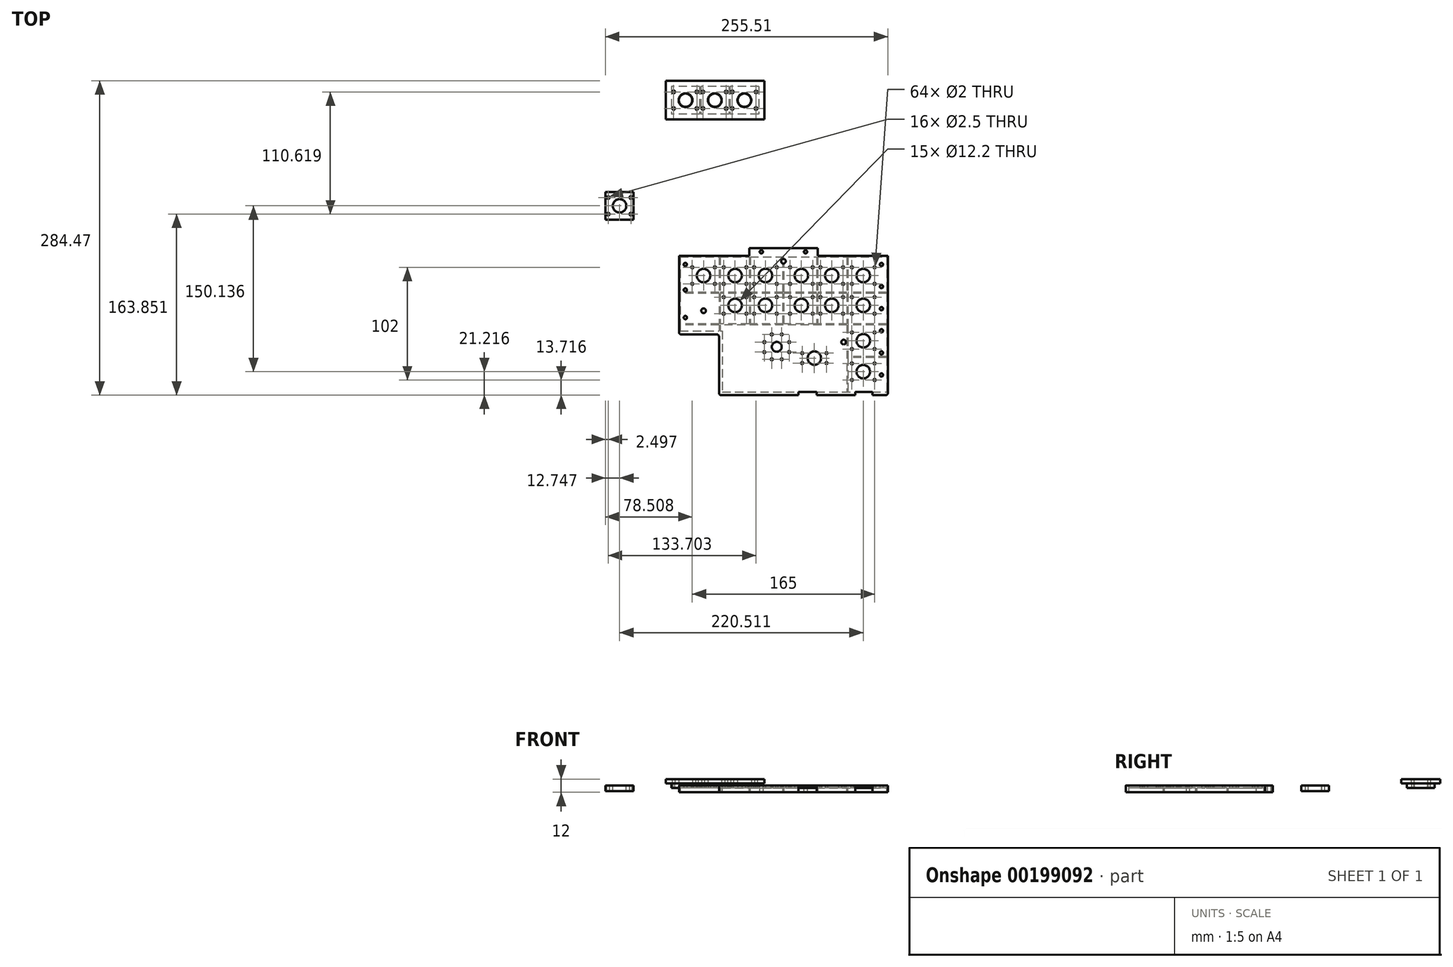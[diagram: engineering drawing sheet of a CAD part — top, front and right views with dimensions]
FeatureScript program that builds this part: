
annotation { "Feature Type Name" : "Feature", "Feature Type Description" : "" }
export const myFeature = defineFeature(function(context is Context, id is Id, definition is map)
    precondition{}
    {
        {
            var Q0;
            Q0=qCreatedBy(makeId("Top.planeOp"),FACE);
            var sketch = newSketch(context, id + "F0", { "sketchPlane" : qUnion([Q0])});
            skLineSegment(sketch, "E0.bottom", {"start": v(7.75, 12.5) * mm, "end": v(-7.75, 12.5) * mm});
            skLineSegment(sketch, "E0.top", {"start": v(7.75, -12.5) * mm, "end": v(-7.75, -12.5) * mm});
            skLineSegment(sketch, "E0.left", {"start": v(7.75, 12.5) * mm, "end": v(7.75, -12.5) * mm});
            skLineSegment(sketch, "E0.right", {"start": v(-7.75, 12.5) * mm, "end": v(-7.75, -12.5) * mm});
            skPoint(sketch, "E0.middle", {"position": v(0, 0) * mm});
            skLineSegment(sketch, "E1.bottom", {"start": v(-7.75, 12.5) * mm, "end": v(-12.75, 12.5) * mm});
            skLineSegment(sketch, "E1.top", {"start": v(-7.75, -12.5) * mm, "end": v(-12.75, -12.5) * mm});
            skLineSegment(sketch, "E1.right", {"start": v(-12.75, 12.5) * mm, "end": v(-12.75, -12.5) * mm});
            skLineSegment(sketch, "E2.bottom", {"start": v(7.75, 12.5) * mm, "end": v(12.75, 12.5) * mm});
            skLineSegment(sketch, "E2.top", {"start": v(7.75, -12.5) * mm, "end": v(12.75, -12.5) * mm});
            skLineSegment(sketch, "E2.right", {"start": v(12.75, 12.5) * mm, "end": v(12.75, -12.5) * mm});
            skCircle(sketch, "E3", {"center": v(-10.75, 7.5) * mm, "radius": 0.9 * mm});
            skPoint(sketch, "E3.centerSnap0", {"position": v(-10.25, 12.5) * mm});
            skCircle(sketch, "E4", {"center": v(-10.75, -7.5) * mm, "radius": 0.9 * mm});
            skCircle(sketch, "E5", {"center": v(10.25, 7.5) * mm, "radius": 0.9 * mm});
            skPoint(sketch, "E5.centerSnap0", {"position": v(10.25, 12.5) * mm});
            skCircle(sketch, "E6", {"center": v(10.25, -7.5) * mm, "radius": 0.9 * mm});
            skCircle(sketch, "E7", {"center": v(0, 0) * mm, "radius": 6 * mm});
            skLineSegment(sketch, "E8.bottom", {"start": v(34.25, 12.5) * mm, "end": v(18.75, 12.5) * mm});
            skLineSegment(sketch, "E8.top", {"start": v(34.25, -12.5) * mm, "end": v(18.75, -12.5) * mm});
            skLineSegment(sketch, "E8.left", {"start": v(34.25, 12.5) * mm, "end": v(34.25, -12.5) * mm});
            skLineSegment(sketch, "E8.right", {"start": v(18.75, 12.5) * mm, "end": v(18.75, -12.5) * mm});
            skPoint(sketch, "E8.middle", {"position": v(26.5, 0) * mm});
            skLineSegment(sketch, "E9.bottom", {"start": v(18.75, 12.5) * mm, "end": v(13.75, 12.5) * mm});
            skLineSegment(sketch, "E9.top", {"start": v(18.75, -12.5) * mm, "end": v(13.75, -12.5) * mm});
            skLineSegment(sketch, "E9.right", {"start": v(13.75, 12.5) * mm, "end": v(13.75, -12.5) * mm});
            skLineSegment(sketch, "E10.bottom", {"start": v(34.25, 12.5) * mm, "end": v(39.25, 12.5) * mm});
            skLineSegment(sketch, "E10.top", {"start": v(34.25, -12.5) * mm, "end": v(39.25, -12.5) * mm});
            skLineSegment(sketch, "E10.right", {"start": v(39.25, 12.5) * mm, "end": v(39.25, -12.5) * mm});
            skCircle(sketch, "E11", {"center": v(15.75, 7.5) * mm, "radius": 0.9 * mm});
            skPoint(sketch, "E11.centerSnap0", {"position": v(16.25, 12.5) * mm});
            skCircle(sketch, "E12", {"center": v(15.75, -7.5) * mm, "radius": 0.9 * mm});
            skCircle(sketch, "E13", {"center": v(36.75, 7.5) * mm, "radius": 0.9 * mm});
            skPoint(sketch, "E13.centerSnap0", {"position": v(36.75, 12.5) * mm});
            skCircle(sketch, "E14", {"center": v(36.75, -7.5) * mm, "radius": 0.9 * mm});
            skCircle(sketch, "E15", {"center": v(26.5, 0) * mm, "radius": 6 * mm});
            skLineSegment(sketch, "E16.bottom", {"start": v(61.25, 12.5) * mm, "end": v(45.25, 12.5) * mm});
            skLineSegment(sketch, "E16.top", {"start": v(61.25, -12.5) * mm, "end": v(45.25, -12.5) * mm});
            skLineSegment(sketch, "E16.left", {"start": v(61.25, 12.5) * mm, "end": v(61.25, -12.5) * mm});
            skLineSegment(sketch, "E16.right", {"start": v(45.25, 12.5) * mm, "end": v(45.25, -12.5) * mm});
            skPoint(sketch, "E16.middle", {"position": v(53.25, 0) * mm});
            skLineSegment(sketch, "E17.bottom", {"start": v(45.25, 12.5) * mm, "end": v(40.25, 12.5) * mm});
            skLineSegment(sketch, "E17.top", {"start": v(45.25, -12.5) * mm, "end": v(40.25, -12.5) * mm});
            skLineSegment(sketch, "E17.right", {"start": v(40.25, 12.5) * mm, "end": v(40.25, -12.5) * mm});
            skLineSegment(sketch, "E18.bottom", {"start": v(61.25, 12.5) * mm, "end": v(66.25, 12.5) * mm});
            skLineSegment(sketch, "E18.top", {"start": v(61.25, -12.5) * mm, "end": v(66.25, -12.5) * mm});
            skLineSegment(sketch, "E18.right", {"start": v(66.25, 12.5) * mm, "end": v(66.25, -12.5) * mm});
            skCircle(sketch, "E19", {"center": v(42.25, 7.5) * mm, "radius": 0.9 * mm});
            skPoint(sketch, "E19.centerSnap0", {"position": v(42.75, 12.5) * mm});
            skCircle(sketch, "E20", {"center": v(42.25, -7.5) * mm, "radius": 0.9 * mm});
            skCircle(sketch, "E21", {"center": v(63.75, 7.5) * mm, "radius": 0.9 * mm});
            skPoint(sketch, "E21.centerSnap0", {"position": v(63.75, 12.5) * mm});
            skCircle(sketch, "E22", {"center": v(63.75, -7.5) * mm, "radius": 0.9 * mm});
            skCircle(sketch, "E23", {"center": v(53.25, 0) * mm, "radius": 6 * mm});
            skSolve(sketch);
        }
        {
            var Q0;
            Q0=makeQuery(id+"F0.imprint","IMPRINT",FACE,{"disambiguationData":[TD([[makeQuery(id+"F0.imprint","IMPRINT",EDGE,{"derivedFrom":sQuery(id+"F0.wireOp",EDGE,"E0.bottom")}),1.0]])]});
            var Q1;
            Q1=makeQuery(id+"F0.imprint","IMPRINT",FACE,{"disambiguationData":[TD([[makeQuery(id+"F0.imprint","IMPRINT",EDGE,{"derivedFrom":sQuery(id+"F0.wireOp",EDGE,"E1.bottom")}),1.0]])]});
            var Q2;
            Q2=makeQuery(id+"F0.imprint","IMPRINT",FACE,{"disambiguationData":[TD([[makeQuery(id+"F0.imprint","IMPRINT",EDGE,{"derivedFrom":sQuery(id+"F0.wireOp",EDGE,"E2.bottom")}),-1.0]])]});
            var Q3;
            Q3=makeQuery(id+"F0.imprint","IMPRINT",FACE,{"disambiguationData":[TD([[makeQuery(id+"F0.imprint","IMPRINT",EDGE,{"derivedFrom":sQuery(id+"F0.wireOp",EDGE,"E9.bottom")}),1.0]])]});
            var Q4;
            Q4=makeQuery(id+"F0.imprint","IMPRINT",FACE,{"disambiguationData":[TD([[makeQuery(id+"F0.imprint","IMPRINT",EDGE,{"derivedFrom":sQuery(id+"F0.wireOp",EDGE,"E8.bottom")}),1.0]])]});
            var Q5;
            Q5=makeQuery(id+"F0.imprint","IMPRINT",FACE,{"disambiguationData":[TD([[makeQuery(id+"F0.imprint","IMPRINT",EDGE,{"derivedFrom":sQuery(id+"F0.wireOp",EDGE,"E10.bottom")}),-1.0]])]});
            var Q6;
            Q6=makeQuery(id+"F0.imprint","IMPRINT",FACE,{"disambiguationData":[TD([[makeQuery(id+"F0.imprint","IMPRINT",EDGE,{"derivedFrom":sQuery(id+"F0.wireOp",EDGE,"E17.bottom")}),1.0]])]});
            var Q7;
            Q7=makeQuery(id+"F0.imprint","IMPRINT",FACE,{"disambiguationData":[TD([[makeQuery(id+"F0.imprint","IMPRINT",EDGE,{"derivedFrom":sQuery(id+"F0.wireOp",EDGE,"E16.bottom")}),1.0]])]});
            var Q8;
            Q8=makeQuery(id+"F0.imprint","IMPRINT",FACE,{"disambiguationData":[TD([[makeQuery(id+"F0.imprint","IMPRINT",EDGE,{"derivedFrom":sQuery(id+"F0.wireOp",EDGE,"E18.bottom")}),-1.0]])]});
            extrude(context, id + "F1", {"entities" : qUnion([Q0, Q1, Q2, Q3, Q4, Q5, Q6, Q7, Q8]), "depth" : 4 * mm});
        }
        {
            var Q0;
            Q0=makeQuery(id+"F1.opExtrude","CAP_FACE",FACE,{"disambiguationData":[OSD([sQuery(id+"F0.wireOp",EDGE,"E0.bottom"),sQuery(id+"F0.wireOp",EDGE,"E0.top"),sQuery(id+"F0.wireOp",EDGE,"E1.bottom"),sQuery(id+"F0.wireOp",EDGE,"E1.top"),sQuery(id+"F0.wireOp",EDGE,"E1.right"),sQuery(id+"F0.wireOp",EDGE,"E2.bottom"),sQuery(id+"F0.wireOp",EDGE,"E2.top"),sQuery(id+"F0.wireOp",EDGE,"E2.right"),sQuery(id+"F0.wireOp",EDGE,"E3"),sQuery(id+"F0.wireOp",EDGE,"E4"),sQuery(id+"F0.wireOp",EDGE,"E5"),sQuery(id+"F0.wireOp",EDGE,"E6"),sQuery(id+"F0.wireOp",EDGE,"E7")])],"isStart":false});
            var sketch = newSketch(context, id + "F2", { "sketchPlane" : qUnion([Q0])});
            skLineSegment(sketch, "E24.bottom", {"start": v(-17.75, 17.5) * mm, "end": v(71.25, 17.5) * mm});
            skLineSegment(sketch, "E24.top", {"start": v(-17.75, -17.5) * mm, "end": v(71.25, -17.5) * mm});
            skLineSegment(sketch, "E24.left", {"start": v(-17.75, 17.5) * mm, "end": v(-17.75, -17.5) * mm});
            skLineSegment(sketch, "E24.right", {"start": v(71.25, 17.5) * mm, "end": v(71.25, -17.5) * mm});
            skCircle(sketch, "E25", {"center": v(-10.75, 7.5) * mm, "radius": 1.25 * mm});
            skCircle(sketch, "E26", {"center": v(-10.75, -7.5) * mm, "radius": 1.25 * mm});
            skCircle(sketch, "E27", {"center": v(10.25, -7.5) * mm, "radius": 1.25 * mm});
            skCircle(sketch, "E28", {"center": v(10.25, 7.5) * mm, "radius": 1.25 * mm});
            skCircle(sketch, "E29", {"center": v(15.75, 7.5) * mm, "radius": 1.25 * mm});
            skCircle(sketch, "E30", {"center": v(15.75, -7.5) * mm, "radius": 1.25 * mm});
            skCircle(sketch, "E31", {"center": v(36.75, -7.5) * mm, "radius": 1.25 * mm});
            skCircle(sketch, "E32", {"center": v(0, 0) * mm, "radius": 6.25 * mm});
            skCircle(sketch, "E33", {"center": v(26.5, 0) * mm, "radius": 6.25 * mm});
            skCircle(sketch, "E34", {"center": v(53.25, 0) * mm, "radius": 6.25 * mm});
            skCircle(sketch, "E35", {"center": v(36.75, 7.5) * mm, "radius": 1.25 * mm});
            skCircle(sketch, "E36", {"center": v(42.25, 7.5) * mm, "radius": 1.25 * mm});
            skCircle(sketch, "E37", {"center": v(42.25, -7.5) * mm, "radius": 1.25 * mm});
            skCircle(sketch, "E38", {"center": v(63.75, 7.5) * mm, "radius": 1.25 * mm});
            skCircle(sketch, "E39", {"center": v(63.75, -7.5) * mm, "radius": 1.25 * mm});
            skSolve(sketch);
        }
        {
            var Q0;
            Q0=qSketchRegion(id+"F2",true);
            extrude(context, id + "F3", {"entities" : qUnion([Q0]), "depth" : 4 * mm});
        }
        {
            var Q0;
            Q0=qCreatedBy(makeId("Top.planeOp"),FACE);
            var sketch = newSketch(context, id + "F4", { "sketchPlane" : qUnion([Q0])});
            skLineSegment(sketch, "E40.bottom", {"start": v(3.56, -143.75) * mm, "end": v(29.06, -143.75) * mm, "construction": true});
            skLineSegment(sketch, "E40.top", {"start": v(3.56, -173.75) * mm, "end": v(29.06, -173.75) * mm, "construction": true});
            skLineSegment(sketch, "E40.left", {"start": v(3.56, -143.75) * mm, "end": v(3.56, -173.75) * mm, "construction": true});
            skLineSegment(sketch, "E40.right", {"start": v(29.06, -143.75) * mm, "end": v(29.06, -173.75) * mm, "construction": true});
            skLineSegment(sketch, "E41.bottom", {"start": v(32.06, -143.75) * mm, "end": v(57.56, -143.75) * mm, "construction": true});
            skLineSegment(sketch, "E41.top", {"start": v(32.06, -173.75) * mm, "end": v(57.56, -173.75) * mm, "construction": true});
            skLineSegment(sketch, "E41.left", {"start": v(32.06, -143.75) * mm, "end": v(32.06, -173.75) * mm, "construction": true});
            skLineSegment(sketch, "E41.right", {"start": v(57.56, -143.75) * mm, "end": v(57.56, -173.75) * mm, "construction": true});
            skLineSegment(sketch, "E42.bottom", {"start": v(119.56, -143.75) * mm, "end": v(145.06, -143.75) * mm, "construction": true});
            skLineSegment(sketch, "E42.top", {"start": v(119.56, -173.75) * mm, "end": v(145.06, -173.75) * mm, "construction": true});
            skLineSegment(sketch, "E42.left", {"start": v(119.56, -143.75) * mm, "end": v(119.56, -173.75) * mm, "construction": true});
            skLineSegment(sketch, "E42.right", {"start": v(145.06, -143.75) * mm, "end": v(145.06, -173.75) * mm, "construction": true});
            skLineSegment(sketch, "E43.bottom", {"start": v(148.06, -143.75) * mm, "end": v(173.56, -143.75) * mm, "construction": true});
            skLineSegment(sketch, "E43.top", {"start": v(148.06, -173.75) * mm, "end": v(173.56, -173.75) * mm, "construction": true});
            skLineSegment(sketch, "E43.left", {"start": v(148.06, -143.75) * mm, "end": v(148.06, -173.75) * mm, "construction": true});
            skLineSegment(sketch, "E43.right", {"start": v(173.56, -143.75) * mm, "end": v(173.56, -173.75) * mm, "construction": true});
            skLineSegment(sketch, "E44.top", {"start": v(148.06, -206.75) * mm, "end": v(173.56, -206.75) * mm, "construction": true});
            skLineSegment(sketch, "E45.bottom", {"start": v(148.06, -209.25) * mm, "end": v(173.56, -209.25) * mm, "construction": true});
            skLineSegment(sketch, "E45.top", {"start": v(148.06, -239.25) * mm, "end": v(173.56, -239.25) * mm, "construction": true});
            skLineSegment(sketch, "E45.left", {"start": v(148.06, -209.25) * mm, "end": v(148.06, -239.25) * mm, "construction": true});
            skLineSegment(sketch, "E45.right", {"start": v(173.56, -209.25) * mm, "end": v(173.56, -239.25) * mm, "construction": true});
            skLineSegment(sketch, "E46.bottom", {"start": v(-4.94, -140.75) * mm, "end": v(182.06, -140.75) * mm});
            skLineSegment(sketch, "E46.top", {"start": v(33.28, -263.97) * mm, "end": v(182.06, -263.97) * mm});
            skLineSegment(sketch, "E46.left", {"start": v(-4.94, -140.75) * mm, "end": v(-4.94, -208.97) * mm});
            skLineSegment(sketch, "E46.right", {"start": v(182.06, -140.75) * mm, "end": v(182.06, -263.97) * mm});
            skLineSegment(sketch, "E47", {"start": v(-4.94, -208.97) * mm, "end": v(33.28, -208.97) * mm});
            skLineSegment(sketch, "E48", {"start": v(33.28, -208.97) * mm, "end": v(33.28, -263.97) * mm});
            skLineSegment(sketch, "E49.bottom", {"start": v(-67.45, -83.12) * mm, "end": v(-51.95, -83.12) * mm});
            skLineSegment(sketch, "E49.top", {"start": v(-67.45, -108.12) * mm, "end": v(-51.95, -108.12) * mm});
            skLineSegment(sketch, "E49.left", {"start": v(-67.45, -83.12) * mm, "end": v(-67.45, -108.12) * mm});
            skLineSegment(sketch, "E49.right", {"start": v(-51.95, -83.12) * mm, "end": v(-51.95, -108.12) * mm});
            skLineSegment(sketch, "E50.bottom", {"start": v(-51.95, -83.12) * mm, "end": v(-46.95, -83.12) * mm});
            skLineSegment(sketch, "E50.top", {"start": v(-51.95, -108.12) * mm, "end": v(-46.95, -108.12) * mm});
            skLineSegment(sketch, "E50.right", {"start": v(-46.95, -83.12) * mm, "end": v(-46.95, -108.12) * mm});
            skLineSegment(sketch, "E51.bottom", {"start": v(-67.45, -83.12) * mm, "end": v(-72.45, -83.12) * mm});
            skLineSegment(sketch, "E51.top", {"start": v(-67.45, -108.12) * mm, "end": v(-72.45, -108.12) * mm});
            skLineSegment(sketch, "E51.right", {"start": v(-72.45, -83.12) * mm, "end": v(-72.45, -108.12) * mm});
            skCircle(sketch, "E52", {"center": v(-59.7, -95.62) * mm, "radius": 6.1 * mm});
            skPoint(sketch, "E52.centerSnap0", {"position": v(-67.45, -95.62) * mm});
            skPoint(sketch, "E52.centerSnap1", {"position": v(-59.7, -83.12) * mm});
            skCircle(sketch, "E53", {"center": v(-69.95, -88.12) * mm, "radius": 1.25 * mm});
            skPoint(sketch, "E53.centerSnap0", {"position": v(-69.95, -83.12) * mm});
            skCircle(sketch, "E54", {"center": v(-69.95, -103.12) * mm, "radius": 1.25 * mm});
            skCircle(sketch, "E55", {"center": v(-49.45, -88.12) * mm, "radius": 1.25 * mm});
            skPoint(sketch, "E55.centerSnap0", {"position": v(-49.45, -83.12) * mm});
            skCircle(sketch, "E56", {"center": v(-49.45, -103.12) * mm, "radius": 1.25 * mm});
            skLineSegment(sketch, "E57.bottom", {"start": v(3.56, -146.25) * mm, "end": v(8.56, -146.25) * mm, "construction": true});
            skLineSegment(sketch, "E57.top", {"start": v(3.56, -171.25) * mm, "end": v(8.56, -171.25) * mm, "construction": true});
            skLineSegment(sketch, "E57.left", {"start": v(3.56, -146.25) * mm, "end": v(3.56, -171.25) * mm, "construction": true});
            skLineSegment(sketch, "E57.right", {"start": v(8.56, -146.25) * mm, "end": v(8.56, -171.25) * mm, "construction": true});
            skLineSegment(sketch, "E58.bottom", {"start": v(29.06, -146.25) * mm, "end": v(24.06, -146.25) * mm, "construction": true});
            skLineSegment(sketch, "E58.top", {"start": v(29.06, -171.25) * mm, "end": v(24.06, -171.25) * mm, "construction": true});
            skLineSegment(sketch, "E58.left", {"start": v(29.06, -146.25) * mm, "end": v(29.06, -171.25) * mm, "construction": true});
            skLineSegment(sketch, "E58.right", {"start": v(24.06, -146.25) * mm, "end": v(24.06, -171.25) * mm, "construction": true});
            skCircle(sketch, "E59", {"center": v(6.06, -151.25) * mm, "radius": 1 * mm});
            skPoint(sketch, "E59.centerSnap0", {"position": v(6.06, -146.25) * mm});
            skCircle(sketch, "E60", {"center": v(6.06, -166.25) * mm, "radius": 1 * mm});
            skCircle(sketch, "E61", {"center": v(16.3, -158.75) * mm, "radius": 6.1 * mm});
            skPoint(sketch, "E61.centerSnap0", {"position": v(8.56, -158.75) * mm});
            skPoint(sketch, "E61.centerSnap1", {"position": v(16.3, -143.75) * mm});
            skCircle(sketch, "E62", {"center": v(26.56, -151.25) * mm, "radius": 1 * mm});
            skPoint(sketch, "E62.centerSnap0", {"position": v(26.56, -146.25) * mm});
            skCircle(sketch, "E63", {"center": v(26.56, -166.25) * mm, "radius": 1 * mm});
            skCircle(sketch, "E64", {"center": v(105.56, -228.97) * mm, "radius": 1 * mm});
            skCircle(sketch, "E65", {"center": v(105.56, -237.97) * mm, "radius": 1 * mm});
            skCircle(sketch, "E66", {"center": v(127.56, -228.97) * mm, "radius": 1 * mm});
            skCircle(sketch, "E67", {"center": v(127.56, -237.97) * mm, "radius": 1 * mm});
            skLineSegment(sketch, "E68.bottom", {"start": v(151.56, -240.25) * mm, "end": v(173.56, -240.25) * mm, "construction": true});
            skLineSegment(sketch, "E68.top", {"start": v(151.56, -262.25) * mm, "end": v(173.56, -262.25) * mm, "construction": true});
            skLineSegment(sketch, "E68.left", {"start": v(151.56, -240.25) * mm, "end": v(151.56, -262.25) * mm, "construction": true});
            skLineSegment(sketch, "E68.right", {"start": v(173.56, -240.25) * mm, "end": v(173.56, -262.25) * mm, "construction": true});
            skLineSegment(sketch, "E69.bottom", {"start": v(154.8, -239.75) * mm, "end": v(166.8, -239.75) * mm, "construction": true});
            skLineSegment(sketch, "E69.top", {"start": v(154.8, -251.75) * mm, "end": v(166.8, -251.75) * mm, "construction": true});
            skLineSegment(sketch, "E69.left", {"start": v(154.8, -239.75) * mm, "end": v(154.8, -251.75) * mm, "construction": true});
            skLineSegment(sketch, "E69.right", {"start": v(166.8, -239.75) * mm, "end": v(166.8, -251.75) * mm, "construction": true});
            skLineSegment(sketch, "E70.bottom", {"start": v(32.06, -146.25) * mm, "end": v(37.06, -146.25) * mm, "construction": true});
            skLineSegment(sketch, "E70.top", {"start": v(32.06, -171.25) * mm, "end": v(37.06, -171.25) * mm, "construction": true});
            skLineSegment(sketch, "E70.left", {"start": v(32.06, -146.25) * mm, "end": v(32.06, -171.25) * mm, "construction": true});
            skLineSegment(sketch, "E70.right", {"start": v(37.06, -146.25) * mm, "end": v(37.06, -171.25) * mm, "construction": true});
            skLineSegment(sketch, "E71.bottom", {"start": v(57.56, -146.25) * mm, "end": v(52.56, -146.25) * mm, "construction": true});
            skLineSegment(sketch, "E71.top", {"start": v(57.56, -171.25) * mm, "end": v(52.56, -171.25) * mm, "construction": true});
            skLineSegment(sketch, "E71.left", {"start": v(57.56, -146.25) * mm, "end": v(57.56, -171.25) * mm, "construction": true});
            skLineSegment(sketch, "E71.right", {"start": v(52.56, -146.25) * mm, "end": v(52.56, -171.25) * mm, "construction": true});
            skCircle(sketch, "E72", {"center": v(34.56, -151.25) * mm, "radius": 1 * mm});
            skPoint(sketch, "E72.centerSnap0", {"position": v(34.56, -146.25) * mm});
            skCircle(sketch, "E73", {"center": v(34.56, -166.25) * mm, "radius": 1 * mm});
            skCircle(sketch, "E74", {"center": v(55.06, -151.25) * mm, "radius": 1 * mm});
            skPoint(sketch, "E74.centerSnap0", {"position": v(55.06, -146.25) * mm});
            skCircle(sketch, "E75", {"center": v(55.06, -166.25) * mm, "radius": 1 * mm});
            skCircle(sketch, "E76", {"center": v(44.8, -158.75) * mm, "radius": 6.1 * mm});
            skPoint(sketch, "E76.centerSnap0", {"position": v(37.06, -158.75) * mm});
            skPoint(sketch, "E76.centerSnap1", {"position": v(44.8, -143.75) * mm});
            skLineSegment(sketch, "E77.bottom", {"start": v(119.56, -146.25) * mm, "end": v(124.56, -146.25) * mm, "construction": true});
            skLineSegment(sketch, "E77.top", {"start": v(119.56, -171.25) * mm, "end": v(124.56, -171.25) * mm, "construction": true});
            skLineSegment(sketch, "E77.left", {"start": v(119.56, -146.25) * mm, "end": v(119.56, -171.25) * mm, "construction": true});
            skLineSegment(sketch, "E77.right", {"start": v(124.56, -146.25) * mm, "end": v(124.56, -171.25) * mm, "construction": true});
            skLineSegment(sketch, "E78.bottom", {"start": v(145.06, -146.25) * mm, "end": v(140.06, -146.25) * mm, "construction": true});
            skLineSegment(sketch, "E78.top", {"start": v(145.06, -171.25) * mm, "end": v(140.06, -171.25) * mm, "construction": true});
            skLineSegment(sketch, "E78.left", {"start": v(145.06, -146.25) * mm, "end": v(145.06, -171.25) * mm, "construction": true});
            skLineSegment(sketch, "E78.right", {"start": v(140.06, -146.25) * mm, "end": v(140.06, -171.25) * mm, "construction": true});
            skLineSegment(sketch, "E79.bottom", {"start": v(148.06, -146.25) * mm, "end": v(153.06, -146.25) * mm, "construction": true});
            skLineSegment(sketch, "E79.top", {"start": v(148.06, -171.25) * mm, "end": v(153.06, -171.25) * mm, "construction": true});
            skLineSegment(sketch, "E79.left", {"start": v(148.06, -146.25) * mm, "end": v(148.06, -171.25) * mm, "construction": true});
            skLineSegment(sketch, "E79.right", {"start": v(153.06, -146.25) * mm, "end": v(153.06, -171.25) * mm, "construction": true});
            skLineSegment(sketch, "E80.bottom", {"start": v(173.56, -146.25) * mm, "end": v(168.56, -146.25) * mm, "construction": true});
            skLineSegment(sketch, "E80.top", {"start": v(173.56, -171.25) * mm, "end": v(168.56, -171.25) * mm, "construction": true});
            skLineSegment(sketch, "E80.left", {"start": v(173.56, -146.25) * mm, "end": v(173.56, -171.25) * mm, "construction": true});
            skLineSegment(sketch, "E80.right", {"start": v(168.56, -146.25) * mm, "end": v(168.56, -171.25) * mm, "construction": true});
            skLineSegment(sketch, "E81.top", {"start": v(148.06, -204.25) * mm, "end": v(153.06, -204.25) * mm, "construction": true});
            skLineSegment(sketch, "E82.top", {"start": v(173.56, -204.25) * mm, "end": v(168.56, -204.25) * mm, "construction": true});
            skLineSegment(sketch, "E83.bottom", {"start": v(148.06, -205.25) * mm, "end": v(153.06, -205.25) * mm, "construction": true});
            skLineSegment(sketch, "E83.top", {"start": v(148.06, -230.25) * mm, "end": v(153.06, -230.25) * mm, "construction": true});
            skLineSegment(sketch, "E83.left", {"start": v(148.06, -205.25) * mm, "end": v(148.06, -230.25) * mm, "construction": true});
            skLineSegment(sketch, "E83.right", {"start": v(153.06, -205.25) * mm, "end": v(153.06, -230.25) * mm, "construction": true});
            skLineSegment(sketch, "E84.bottom", {"start": v(173.56, -205.25) * mm, "end": v(168.56, -205.25) * mm, "construction": true});
            skLineSegment(sketch, "E84.top", {"start": v(173.56, -230.25) * mm, "end": v(168.56, -230.25) * mm, "construction": true});
            skLineSegment(sketch, "E84.left", {"start": v(173.56, -205.25) * mm, "end": v(173.56, -230.25) * mm, "construction": true});
            skLineSegment(sketch, "E84.right", {"start": v(168.56, -205.25) * mm, "end": v(168.56, -230.25) * mm, "construction": true});
            skCircle(sketch, "E85", {"center": v(62.06, -178.25) * mm, "radius": 1 * mm});
            skCircle(sketch, "E86", {"center": v(62.06, -193.25) * mm, "radius": 1 * mm});
            skCircle(sketch, "E87", {"center": v(82.56, -178.25) * mm, "radius": 1 * mm});
            skCircle(sketch, "E88", {"center": v(82.56, -193.25) * mm, "radius": 1 * mm});
            skCircle(sketch, "E89", {"center": v(72.3, -185.75) * mm, "radius": 6.1 * mm});
            skCircle(sketch, "E90", {"center": v(82.56, -223.25) * mm, "radius": 4.5 * mm});
            skCircle(sketch, "E91", {"center": v(71.3, -219) * mm, "radius": 1 * mm});
            skCircle(sketch, "E92", {"center": v(71.3, -228) * mm, "radius": 1 * mm});
            skCircle(sketch, "E93", {"center": v(93.8, -219) * mm, "radius": 1 * mm});
            skCircle(sketch, "E94", {"center": v(93.8, -228) * mm, "radius": 1 * mm});
            skCircle(sketch, "E95", {"center": v(94.56, -178.25) * mm, "radius": 1 * mm});
            skCircle(sketch, "E96", {"center": v(94.56, -193.25) * mm, "radius": 1 * mm});
            skCircle(sketch, "E97", {"center": v(115.06, -178.25) * mm, "radius": 1 * mm});
            skCircle(sketch, "E98", {"center": v(115.06, -193.25) * mm, "radius": 1 * mm});
            skCircle(sketch, "E99", {"center": v(122.06, -151.25) * mm, "radius": 1 * mm});
            skPoint(sketch, "E99.centerSnap0", {"position": v(122.06, -146.25) * mm});
            skCircle(sketch, "E100", {"center": v(122.06, -166.25) * mm, "radius": 1 * mm});
            skCircle(sketch, "E101", {"center": v(132.3, -158.75) * mm, "radius": 6.1 * mm});
            skPoint(sketch, "E101.centerSnap0", {"position": v(124.56, -158.75) * mm});
            skPoint(sketch, "E101.centerSnap1", {"position": v(132.3, -143.75) * mm});
            skCircle(sketch, "E102", {"center": v(142.56, -151.25) * mm, "radius": 1 * mm});
            skPoint(sketch, "E102.centerSnap0", {"position": v(142.56, -146.25) * mm});
            skCircle(sketch, "E103", {"center": v(142.56, -166.25) * mm, "radius": 1 * mm});
            skCircle(sketch, "E104", {"center": v(150.56, -151.25) * mm, "radius": 1 * mm});
            skPoint(sketch, "E104.centerSnap0", {"position": v(150.56, -146.25) * mm});
            skCircle(sketch, "E105", {"center": v(150.56, -166.25) * mm, "radius": 1 * mm});
            skCircle(sketch, "E106", {"center": v(171.06, -151.25) * mm, "radius": 1 * mm});
            skPoint(sketch, "E106.centerSnap0", {"position": v(171.06, -146.25) * mm});
            skCircle(sketch, "E107", {"center": v(171.06, -166.25) * mm, "radius": 1 * mm});
            skCircle(sketch, "E108", {"center": v(160.8, -158.75) * mm, "radius": 6.1 * mm});
            skPoint(sketch, "E108.centerSnap0", {"position": v(153.06, -158.75) * mm});
            skPoint(sketch, "E108.centerSnap1", {"position": v(160.8, -143.75) * mm});
            skCircle(sketch, "E109", {"center": v(16.3, -190.57) * mm, "radius": 2.1 * mm});
            skCircle(sketch, "E110", {"center": v(143.06, -218.97) * mm, "radius": 2.1 * mm});
            skCircle(sketch, "E111", {"center": v(150.56, -210.25) * mm, "radius": 1 * mm});
            skPoint(sketch, "E111.centerSnap0", {"position": v(150.56, -205.25) * mm});
            skCircle(sketch, "E112", {"center": v(150.56, -225.25) * mm, "radius": 1 * mm});
            skCircle(sketch, "E113", {"center": v(171.06, -210.25) * mm, "radius": 1 * mm});
            skPoint(sketch, "E113.centerSnap0", {"position": v(171.06, -205.25) * mm});
            skCircle(sketch, "E114", {"center": v(171.06, -225.25) * mm, "radius": 1 * mm});
            skCircle(sketch, "E115", {"center": v(160.8, -217.75) * mm, "radius": 6.1 * mm});
            skPoint(sketch, "E115.centerSnap0", {"position": v(153.06, -217.75) * mm});
            skCircle(sketch, "E116", {"center": v(160.8, -245.75) * mm, "radius": 6.1 * mm});
            skPoint(sketch, "E116.centerSnap0", {"position": v(160.8, -239.75) * mm});
            skPoint(sketch, "E116.centerSnap1", {"position": v(154.8, -245.75) * mm});
            skCircle(sketch, "E117", {"center": v(-0.2, -148.75) * mm, "radius": 1.5 * mm});
            skCircle(sketch, "E118", {"center": v(-0.2, -171.75) * mm, "radius": 1.5 * mm});
            skCircle(sketch, "E119", {"center": v(177.3, -208.75) * mm, "radius": 1.5 * mm});
            skCircle(sketch, "E120", {"center": v(177.3, -228.75) * mm, "radius": 1.5 * mm});
            skCircle(sketch, "E121", {"center": v(177.3, -248.75) * mm, "radius": 1.5 * mm});
            skCircle(sketch, "E122", {"center": v(177.3, -168.75) * mm, "radius": 1.5 * mm});
            skCircle(sketch, "E123", {"center": v(177.3, -188.75) * mm, "radius": 1.5 * mm});
            skCircle(sketch, "E124", {"center": v(177.3, -148.75) * mm, "radius": 1.5 * mm});
            skCircle(sketch, "E125", {"center": v(150.56, -238.25) * mm, "radius": 1 * mm});
            skCircle(sketch, "E126", {"center": v(150.56, -253.25) * mm, "radius": 1 * mm});
            skCircle(sketch, "E127", {"center": v(171.06, -238.25) * mm, "radius": 1 * mm});
            skCircle(sketch, "E128", {"center": v(171.06, -253.25) * mm, "radius": 1 * mm});
            skCircle(sketch, "E129", {"center": v(-0.2, -196.75) * mm, "radius": 1.5 * mm});
            skLineSegment(sketch, "E130.bottom", {"start": v(58.56, -140.75) * mm, "end": v(118.56, -140.75) * mm});
            skLineSegment(sketch, "E130.top", {"start": v(58.56, -133.75) * mm, "end": v(118.56, -133.75) * mm});
            skLineSegment(sketch, "E130.left", {"start": v(58.56, -140.75) * mm, "end": v(58.56, -133.75) * mm});
            skLineSegment(sketch, "E130.right", {"start": v(118.56, -140.75) * mm, "end": v(118.56, -133.75) * mm});
            skCircle(sketch, "E131", {"center": v(68.56, -137.25) * mm, "radius": 1.5 * mm});
            skCircle(sketch, "E132", {"center": v(108.56, -137.25) * mm, "radius": 1.5 * mm});
            skCircle(sketch, "E133", {"center": v(116.56, -233.47) * mm, "radius": 6.1 * mm});
            skCircle(sketch, "E134", {"center": v(82.56, -223.25) * mm, "radius": 12.5 * mm, "construction": true});
            skCircle(sketch, "E135", {"center": v(44.8, -185.75) * mm, "radius": 6.1 * mm});
            skCircle(sketch, "E136", {"center": v(34.56, -178.25) * mm, "radius": 1 * mm});
            skCircle(sketch, "E137", {"center": v(34.56, -193.25) * mm, "radius": 1 * mm});
            skCircle(sketch, "E138", {"center": v(55.06, -178.25) * mm, "radius": 1 * mm});
            skCircle(sketch, "E139", {"center": v(55.06, -193.25) * mm, "radius": 1 * mm});
            skCircle(sketch, "E140", {"center": v(122.06, -193.25) * mm, "radius": 1 * mm});
            skCircle(sketch, "E141", {"center": v(142.56, -193.25) * mm, "radius": 1 * mm});
            skLineSegment(sketch, "E142", {"start": v(223.04, -262.25) * mm, "end": v(194.25, -262.25) * mm, "construction": true});
            skCircle(sketch, "E143", {"center": v(78.06, -212) * mm, "radius": 1 * mm});
            skCircle(sketch, "E144", {"center": v(87.06, -212) * mm, "radius": 1 * mm});
            skCircle(sketch, "E145", {"center": v(78.06, -234.5) * mm, "radius": 1 * mm});
            skCircle(sketch, "E146", {"center": v(87.06, -234.5) * mm, "radius": 1 * mm});
            skCircle(sketch, "E147", {"center": v(104.8, -185.75) * mm, "radius": 6.1 * mm});
            skCircle(sketch, "E148", {"center": v(132.3, -185.75) * mm, "radius": 6.1 * mm});
            skCircle(sketch, "E149", {"center": v(122.06, -178.25) * mm, "radius": 1 * mm});
            skCircle(sketch, "E150", {"center": v(142.56, -178.25) * mm, "radius": 1 * mm});
            skCircle(sketch, "E151", {"center": v(160.8, -185.75) * mm, "radius": 6.1 * mm});
            skCircle(sketch, "E152", {"center": v(150.56, -178.25) * mm, "radius": 1 * mm});
            skCircle(sketch, "E153", {"center": v(150.56, -193.25) * mm, "radius": 1 * mm});
            skCircle(sketch, "E154", {"center": v(171.06, -178.25) * mm, "radius": 1 * mm});
            skPoint(sketch, "E154.centerSnap0", {"position": v(171.06, -171.25) * mm});
            skCircle(sketch, "E155", {"center": v(171.06, -193.25) * mm, "radius": 1 * mm});
            skCircle(sketch, "E156", {"center": v(104.8, -158.75) * mm, "radius": 6.1 * mm});
            skCircle(sketch, "E157", {"center": v(115.06, -151.25) * mm, "radius": 1 * mm});
            skCircle(sketch, "E158", {"center": v(115.06, -166.25) * mm, "radius": 1 * mm});
            skCircle(sketch, "E159", {"center": v(94.56, -151.25) * mm, "radius": 1 * mm});
            skCircle(sketch, "E160", {"center": v(94.56, -166.25) * mm, "radius": 1 * mm});
            skCircle(sketch, "E161", {"center": v(72.3, -158.75) * mm, "radius": 6.1 * mm});
            skCircle(sketch, "E162", {"center": v(82.56, -151.25) * mm, "radius": 1 * mm});
            skCircle(sketch, "E163", {"center": v(82.56, -166.25) * mm, "radius": 1 * mm});
            skCircle(sketch, "E164", {"center": v(62.06, -151.25) * mm, "radius": 1 * mm});
            skCircle(sketch, "E165", {"center": v(62.06, -166.25) * mm, "radius": 1 * mm});
            skCircle(sketch, "E166", {"center": v(88.56, -145.75) * mm, "radius": 2.1 * mm});
            skSolve(sketch);
        }
        {
            var Q0;
            Q0=makeQuery(id+"F4.imprint","IMPRINT",FACE,{"disambiguationData":[TD([[makeQuery(id+"F4.imprint","IMPRINT",EDGE,{"derivedFrom":sQuery(id+"F4.wireOp",EDGE,"E49.bottom")}),-1.0]])]});
            var Q1;
            Q1=makeQuery(id+"F4.imprint","IMPRINT",FACE,{"disambiguationData":[TD([[makeQuery(id+"F4.imprint","IMPRINT",EDGE,{"derivedFrom":sQuery(id+"F4.wireOp",EDGE,"E51.bottom")}),1.0]])]});
            var Q2;
            Q2=makeQuery(id+"F4.imprint","IMPRINT",FACE,{"disambiguationData":[TD([[makeQuery(id+"F4.imprint","IMPRINT",EDGE,{"derivedFrom":sQuery(id+"F4.wireOp",EDGE,"E50.bottom")}),-1.0]])]});
            extrude(context, id + "F5", {"entities" : qUnion([Q0, Q1, Q2]), "oppositeDirection" : true, "depth" : 3 * mm});
        }
        {
            var Q0;
            Q0 = qSketchRegion(id + "F4", true);
            extrude(context, id + "F6", {"entities" : qUnion([Q0]), "operationType" : NewBodyOperationType.ADD, "depth" : 2 * mm});
        }
        {
            var Q0;
            Q0=makeQuery(id+"F4.imprint","IMPRINT",FACE,{"disambiguationData":[TD([[makeQuery(id+"F4.imprint","IMPRINT",EDGE,{"derivedFrom":sQuery(id+"F4.wireOp",EDGE,"E46.bottom")}),-1.0]])]});
            var sketch = newSketch(context, id + "F7", { "sketchPlane" : qUnion([Q0])});
            skLineSegment(sketch, "E167", {"start": v(191, -174) * mm, "end": v(196.06, -174) * mm, "construction": true});
            skLineSegment(sketch, "E168", {"start": v(187.13, -202.5) * mm, "end": v(195.16, -202.5) * mm, "construction": true});
            skLineSegment(sketch, "E169", {"start": v(185.67, -231.87) * mm, "end": v(191.23, -231.87) * mm, "construction": true});
            skLineSegment(sketch, "E170", {"start": v(147.06, -137.55) * mm, "end": v(147.06, -134.13) * mm, "construction": true});
            skLineSegment(sketch, "E171", {"start": v(119.6, -132.5) * mm, "end": v(119.6, -129.45) * mm, "construction": true});
            skLineSegment(sketch, "E172", {"start": v(58.56, -132.83) * mm, "end": v(58.56, -129.85) * mm, "construction": true});
            skLineSegment(sketch, "E173", {"start": v(31.28, -136.19) * mm, "end": v(31.28, -132.5) * mm, "construction": true});
            skLineSegment(sketch, "E174.bottom", {"start": v(182.06, -174) * mm, "end": v(147.06, -174) * mm});
            skLineSegment(sketch, "E174.top", {"start": v(182.06, -175) * mm, "end": v(147.06, -175) * mm});
            skLineSegment(sketch, "E174.left", {"start": v(182.06, -174) * mm, "end": v(182.06, -175) * mm});
            skLineSegment(sketch, "E174.right", {"start": v(-4.94, -174) * mm, "end": v(-4.94, -175) * mm});
            skLineSegment(sketch, "E175.bottom", {"start": v(182.06, -202.5) * mm, "end": v(147.06, -202.5) * mm});
            skLineSegment(sketch, "E175.top", {"start": v(182.06, -203.5) * mm, "end": v(147.06, -203.5) * mm});
            skLineSegment(sketch, "E175.left", {"start": v(182.06, -202.5) * mm, "end": v(182.06, -203.5) * mm});
            skLineSegment(sketch, "E175.right", {"start": v(-4.94, -202.5) * mm, "end": v(-4.94, -203.5) * mm});
            skLineSegment(sketch, "E176", {"start": v(194.32, -140.75) * mm, "end": v(196.06, -263.96) * mm, "construction": true});
            skLineSegment(sketch, "E177", {"start": v(190.9, -263.96) * mm, "end": v(185.03, -263.96) * mm, "construction": true});
            skLineSegment(sketch, "E178.bottom", {"start": v(182.06, -231.87) * mm, "end": v(147.06, -231.87) * mm});
            skLineSegment(sketch, "E178.top", {"start": v(182.06, -232.87) * mm, "end": v(147.06, -232.87) * mm});
            skLineSegment(sketch, "E178.left", {"start": v(182.06, -231.87) * mm, "end": v(182.06, -232.87) * mm});
            skLineSegment(sketch, "E179", {"start": v(-4.94, -139.37) * mm, "end": v(-4.94, -137.02) * mm, "construction": true});
            skLineSegment(sketch, "E180", {"start": v(-7.3, -140.75) * mm, "end": v(-12.92, -140.75) * mm, "construction": true});
            skLineSegment(sketch, "E181.bottom", {"start": v(-4.94, -140.75) * mm, "end": v(146.06, -140.75) * mm});
            skLineSegment(sketch, "E181.top", {"start": v(-4.94, -141.75) * mm, "end": v(146.06, -141.75) * mm});
            skLineSegment(sketch, "E181.left", {"start": v(-4.94, -140.75) * mm, "end": v(-4.94, -141.75) * mm});
            skLineSegment(sketch, "E181.right", {"start": v(182.06, -140.75) * mm, "end": v(182.06, -141.75) * mm});
            skLineSegment(sketch, "E182.bottom", {"start": v(147.06, -140.75) * mm, "end": v(146.06, -140.75) * mm});
            skLineSegment(sketch, "E182.top", {"start": v(147.06, -263.96) * mm, "end": v(146.06, -263.96) * mm});
            skLineSegment(sketch, "E182.left", {"start": v(147.06, -141.75) * mm, "end": v(147.06, -174) * mm});
            skLineSegment(sketch, "E182.right", {"start": v(146.06, -141.75) * mm, "end": v(146.06, -174) * mm});
            skLineSegment(sketch, "E183.trimOffspring", {"start": v(147.06, -175) * mm, "end": v(147.06, -202.5) * mm});
            skLineSegment(sketch, "E184.trimOffspring", {"start": v(146.06, -174) * mm, "end": v(119.6, -174) * mm});
            skLineSegment(sketch, "E185.trimOffspring", {"start": v(146.06, -175) * mm, "end": v(146.06, -202.5) * mm});
            skLineSegment(sketch, "E186.trimOffspring", {"start": v(146.06, -175) * mm, "end": v(119.6, -175) * mm});
            skLineSegment(sketch, "E187.trimOffspring", {"start": v(146.06, -202.5) * mm, "end": v(119.6, -202.5) * mm});
            skLineSegment(sketch, "E188.trimOffspring", {"start": v(147.06, -203.5) * mm, "end": v(147.06, -231.87) * mm});
            skLineSegment(sketch, "E189.trimOffspring", {"start": v(146.06, -203.5) * mm, "end": v(58.56, -203.5) * mm});
            skLineSegment(sketch, "E190.trimOffspring", {"start": v(146.06, -203.5) * mm, "end": v(146.06, -263.96) * mm});
            skLineSegment(sketch, "E191.trimOffspring", {"start": v(147.06, -232.87) * mm, "end": v(147.06, -263.96) * mm});
            skLineSegment(sketch, "E192.trimOffspring", {"start": v(147.06, -140.75) * mm, "end": v(182.06, -140.75) * mm});
            skLineSegment(sketch, "E193.trimOffspring", {"start": v(147.06, -141.75) * mm, "end": v(182.06, -141.75) * mm});
            skLineSegment(sketch, "E194.bottom", {"start": v(119.6, -140.75) * mm, "end": v(118.6, -140.75) * mm});
            skLineSegment(sketch, "E194.left", {"start": v(119.6, -140.75) * mm, "end": v(119.6, -174) * mm});
            skLineSegment(sketch, "E194.right", {"start": v(118.6, -140.75) * mm, "end": v(118.6, -174) * mm});
            skLineSegment(sketch, "E195.top", {"start": v(89.06, -148.72) * mm, "end": v(88.06, -148.72) * mm});
            skLineSegment(sketch, "E195.left", {"start": v(89.06, -202.5) * mm, "end": v(89.06, -175) * mm});
            skLineSegment(sketch, "E195.right", {"start": v(88.06, -202.5) * mm, "end": v(88.06, -175) * mm});
            skLineSegment(sketch, "E196.bottom", {"start": v(58.56, -140.75) * mm, "end": v(57.56, -140.75) * mm});
            skLineSegment(sketch, "E196.left", {"start": v(58.56, -140.75) * mm, "end": v(58.56, -174) * mm});
            skLineSegment(sketch, "E196.right", {"start": v(57.56, -140.75) * mm, "end": v(57.56, -174) * mm});
            skLineSegment(sketch, "E197.trimOffspring", {"start": v(119.6, -175) * mm, "end": v(119.6, -202.5) * mm});
            skLineSegment(sketch, "E198.trimOffspring", {"start": v(118.6, -174) * mm, "end": v(89.06, -174) * mm});
            skLineSegment(sketch, "E199.trimOffspring", {"start": v(118.6, -175) * mm, "end": v(118.6, -202.5) * mm});
            skLineSegment(sketch, "E200.trimOffspring", {"start": v(118.6, -175) * mm, "end": v(89.06, -175) * mm});
            skLineSegment(sketch, "E201.trimOffspring", {"start": v(89.06, -174) * mm, "end": v(89.06, -148.72) * mm});
            skLineSegment(sketch, "E202.trimOffspring", {"start": v(88.06, -174) * mm, "end": v(58.56, -174) * mm});
            skLineSegment(sketch, "E203.trimOffspring", {"start": v(88.06, -174) * mm, "end": v(88.06, -148.72) * mm});
            skLineSegment(sketch, "E204.trimOffspring", {"start": v(88.06, -175) * mm, "end": v(58.56, -175) * mm});
            skLineSegment(sketch, "E205.trimOffspring", {"start": v(88.06, -202.5) * mm, "end": v(58.56, -202.5) * mm});
            skLineSegment(sketch, "E206.trimOffspring", {"start": v(118.6, -202.5) * mm, "end": v(89.06, -202.5) * mm});
            skLineSegment(sketch, "E207.bottom", {"start": v(31.28, -140.75) * mm, "end": v(30.28, -140.75) * mm});
            skLineSegment(sketch, "E207.left", {"start": v(31.28, -140.75) * mm, "end": v(31.28, -174) * mm});
            skLineSegment(sketch, "E207.right", {"start": v(30.28, -140.75) * mm, "end": v(30.28, -174) * mm});
            skLineSegment(sketch, "E208.trimOffspring", {"start": v(57.56, -202.5) * mm, "end": v(31.28, -202.5) * mm});
            skLineSegment(sketch, "E209.trimOffspring", {"start": v(58.56, -203.5) * mm, "end": v(31.28, -203.5) * mm});
            skLineSegment(sketch, "E210.trimOffspring", {"start": v(58.56, -175) * mm, "end": v(58.56, -202.5) * mm});
            skLineSegment(sketch, "E211.trimOffspring", {"start": v(57.56, -174) * mm, "end": v(31.28, -174) * mm});
            skLineSegment(sketch, "E212.trimOffspring", {"start": v(57.56, -175) * mm, "end": v(57.56, -202.5) * mm});
            skLineSegment(sketch, "E213.trimOffspring", {"start": v(57.56, -175) * mm, "end": v(31.28, -175) * mm});
            skLineSegment(sketch, "E214.trimOffspring", {"start": v(31.28, -175) * mm, "end": v(31.28, -202.5) * mm});
            skLineSegment(sketch, "E215.trimOffspring", {"start": v(30.28, -174) * mm, "end": v(-4.94, -174) * mm});
            skLineSegment(sketch, "E216.trimOffspring", {"start": v(30.28, -175) * mm, "end": v(30.28, -202.5) * mm});
            skLineSegment(sketch, "E217.trimOffspring", {"start": v(30.28, -175) * mm, "end": v(-4.94, -175) * mm});
            skLineSegment(sketch, "E218.trimOffspring", {"start": v(30.28, -202.5) * mm, "end": v(-4.94, -202.5) * mm});
            skLineSegment(sketch, "E219.top", {"start": v(31.28, -208.97) * mm, "end": v(30.28, -208.97) * mm});
            skLineSegment(sketch, "E219.left", {"start": v(31.28, -203.5) * mm, "end": v(31.28, -208.97) * mm});
            skLineSegment(sketch, "E219.right", {"start": v(30.28, -203.5) * mm, "end": v(30.28, -208.97) * mm});
            skLineSegment(sketch, "E220.trimOffspring", {"start": v(30.28, -203.5) * mm, "end": v(-4.94, -203.5) * mm});
            skLineSegment(sketch, "E221.bottom", {"start": v(99.56, -203.5) * mm, "end": v(98.56, -203.5) * mm});
            skSolve(sketch);
        }
        {
            var Q0;
            Q0=makeQuery(id+"F6.opExtrude","CAP_FACE",FACE,{"disambiguationData":[OSD([sQuery(id+"F4.wireOp",EDGE,"E46.bottom"),sQuery(id+"F4.wireOp",EDGE,"E46.top"),sQuery(id+"F4.wireOp",EDGE,"E46.left"),sQuery(id+"F4.wireOp",EDGE,"E46.right"),sQuery(id+"F4.wireOp",EDGE,"E47"),sQuery(id+"F4.wireOp",EDGE,"E48"),sQuery(id+"F4.wireOp",EDGE,"E59"),sQuery(id+"F4.wireOp",EDGE,"E60"),sQuery(id+"F4.wireOp",EDGE,"E61"),sQuery(id+"F4.wireOp",EDGE,"E62"),sQuery(id+"F4.wireOp",EDGE,"E63"),sQuery(id+"F4.wireOp",EDGE,"E64"),sQuery(id+"F4.wireOp",EDGE,"E65"),sQuery(id+"F4.wireOp",EDGE,"E66"),sQuery(id+"F4.wireOp",EDGE,"E67"),sQuery(id+"F4.wireOp",EDGE,"E72"),sQuery(id+"F4.wireOp",EDGE,"E73"),sQuery(id+"F4.wireOp",EDGE,"E74"),sQuery(id+"F4.wireOp",EDGE,"E75"),sQuery(id+"F4.wireOp",EDGE,"E76"),sQuery(id+"F4.wireOp",EDGE,"CMYmPeaI-4HkP-dSsT-ciCo-EBNArNxvabU4"),sQuery(id+"F4.wireOp",EDGE,"UfYHLVnG-ZsXc-hSsb-096B-xReGw4xjWMuN"),sQuery(id+"F4.wireOp",EDGE,"LR1Smqzz-4zCy-jBud-aIPe-T4FdCvFcucQ2"),sQuery(id+"F4.wireOp",EDGE,"ZbBtRst9-qfY5-xJJi-duYC-lclwT5zfDQth"),sQuery(id+"F4.wireOp",EDGE,"8mlmSCBx-nmsO-8ibw-fLZu-H13SXNY5Fta6"),sQuery(id+"F4.wireOp",EDGE,"E85"),sQuery(id+"F4.wireOp",EDGE,"E86"),sQuery(id+"F4.wireOp",EDGE,"E87"),sQuery(id+"F4.wireOp",EDGE,"E88"),sQuery(id+"F4.wireOp",EDGE,"E89"),sQuery(id+"F4.wireOp",EDGE,"E90"),sQuery(id+"F4.wireOp",EDGE,"E91"),sQuery(id+"F4.wireOp",EDGE,"E92"),sQuery(id+"F4.wireOp",EDGE,"E93"),sQuery(id+"F4.wireOp",EDGE,"E94"),sQuery(id+"F4.wireOp",EDGE,"VxGM9Us5-GGZY-iukY-QufE-Hgw7Eb7M8YLq"),sQuery(id+"F4.wireOp",EDGE,"SQwhu13T-8Qlf-M2A9-FjbU-sqE2fhrdCHsq"),sQuery(id+"F4.wireOp",EDGE,"boMX5wRL-iCUG-njbD-9Rz0-iznqWW2C3mA9"),sQuery(id+"F4.wireOp",EDGE,"8wUrnrco-ptQb-soB3-ZJPL-oLVazxcvUS0h"),sQuery(id+"F4.wireOp",EDGE,"HpmNjthl-ehj3-1CQD-7Ubw-BaRG0imoQFcp"),sQuery(id+"F4.wireOp",EDGE,"E95"),sQuery(id+"F4.wireOp",EDGE,"E96"),sQuery(id+"F4.wireOp",EDGE,"E97"),sQuery(id+"F4.wireOp",EDGE,"E98"),sQuery(id+"F4.wireOp",EDGE,"VaTJDDM9-VUwq-8Ub5-B3vK-8OZuGjwCmtKx"),sQuery(id+"F4.wireOp",EDGE,"E99"),sQuery(id+"F4.wireOp",EDGE,"E100"),sQuery(id+"F4.wireOp",EDGE,"E101"),sQuery(id+"F4.wireOp",EDGE,"E102"),sQuery(id+"F4.wireOp",EDGE,"E103"),sQuery(id+"F4.wireOp",EDGE,"E104"),sQuery(id+"F4.wireOp",EDGE,"E105"),sQuery(id+"F4.wireOp",EDGE,"E106"),sQuery(id+"F4.wireOp",EDGE,"E107"),sQuery(id+"F4.wireOp",EDGE,"E108"),sQuery(id+"F4.wireOp",EDGE,"FLjO8hJO-b9aV-ejTu-NQdn-92oojDJo2zOz"),sQuery(id+"F4.wireOp",EDGE,"a0hJ5jbA-nbqK-hj7D-t7WL-IcpDiukpPwzh"),sQuery(id+"F4.wireOp",EDGE,"Ryervvjx-vNoG-fDVS-CNAW-2For5iN3UFYN"),sQuery(id+"F4.wireOp",EDGE,"h7MID1Gx-mTQT-Sx65-6Eka-E6sNebulpS2X"),sQuery(id+"F4.wireOp",EDGE,"WRXfD2HC-k7r3-eJkd-8mHz-8ZkhsYc1BRgL"),sQuery(id+"F4.wireOp",EDGE,"E109"),sQuery(id+"F4.wireOp",EDGE,"E110"),sQuery(id+"F4.wireOp",EDGE,"E111"),sQuery(id+"F4.wireOp",EDGE,"E112"),sQuery(id+"F4.wireOp",EDGE,"E113"),sQuery(id+"F4.wireOp",EDGE,"E114"),sQuery(id+"F4.wireOp",EDGE,"E115"),sQuery(id+"F4.wireOp",EDGE,"i2m1gv8j-diLw-4k4K-fPdu-nWKSfx8HA4P4"),sQuery(id+"F4.wireOp",EDGE,"q3kUeOFW-MYc1-yF3y-feIh-HT3K9hYQvfPw"),sQuery(id+"F4.wireOp",EDGE,"E116"),sQuery(id+"F4.wireOp",EDGE,"0s6mQaFc-8NzZ-X89h-nX0r-AyVE9FRU5R3i"),sQuery(id+"F4.wireOp",EDGE,"E117"),sQuery(id+"F4.wireOp",EDGE,"OnnnS06f-s26S-AFDA-oTM6-wnMq7venfp2T"),sQuery(id+"F4.wireOp",EDGE,"V2efC4Jm-4NAF-VBiO-pQnY-etMWDclGv5un"),sQuery(id+"F4.wireOp",EDGE,"E118"),sQuery(id+"F4.wireOp",EDGE,"7M3HGg5D-aMQl-LYs1-MsCg-zVmLHFwYCo0C"),sQuery(id+"F4.wireOp",EDGE,"e6U4q213-1LtL-vwCs-wLTg-mGHH5etSdpE2"),sQuery(id+"F4.wireOp",EDGE,"E119"),sQuery(id+"F4.wireOp",EDGE,"E120"),sQuery(id+"F4.wireOp",EDGE,"E121"),sQuery(id+"F4.wireOp",EDGE,"E122"),sQuery(id+"F4.wireOp",EDGE,"R6Wk8btU-zCGi-4TmP-5Jjd-FV93XaIFImrj"),sQuery(id+"F4.wireOp",EDGE,"E123"),sQuery(id+"F4.wireOp",EDGE,"E124"),sQuery(id+"F4.wireOp",EDGE,"gRVzFYeP-EyGY-z86r-QQTZ-wZyysSSB34M7"),sQuery(id+"F4.wireOp",EDGE,"ylX56w3w-VO5M-fSch-uKYX-FYdjN5tmCMk0"),sQuery(id+"F4.wireOp",EDGE,"agFm78Yh-b6q2-hou8-vdYd-aVKsI7ZKnxmv"),sQuery(id+"F4.wireOp",EDGE,"Ipsl4LbN-QmTd-Wo4k-Iefa-eoOeaxQxMcxx"),sQuery(id+"F4.wireOp",EDGE,"aOvKBL3Z-v0oe-Nazm-0AOk-5JJxyVFELpqL"),sQuery(id+"F4.wireOp",EDGE,"PIPjAFRf-HRrE-UI3a-6rHr-U4BEnBnb3Jr0"),sQuery(id+"F4.wireOp",EDGE,"clCWdQkL-82pP-eXah-HGsn-A5WvFmz6JLAg"),sQuery(id+"F4.wireOp",EDGE,"E125"),sQuery(id+"F4.wireOp",EDGE,"E126"),sQuery(id+"F4.wireOp",EDGE,"E127"),sQuery(id+"F4.wireOp",EDGE,"E128"),sQuery(id+"F4.wireOp",EDGE,"2CZ2vCPZ-g25f-Aix0-Xy3j-dVw2FXJ3BshQ.bottom"),sQuery(id+"F4.wireOp",EDGE,"2CZ2vCPZ-g25f-Aix0-Xy3j-dVw2FXJ3BshQ.left"),sQuery(id+"F4.wireOp",EDGE,"2CZ2vCPZ-g25f-Aix0-Xy3j-dVw2FXJ3BshQ.right"),sQuery(id+"F4.wireOp",EDGE,"3PAsEz4y-MCME-JD8k-KRcV-DaMAZ5aYk3wh"),sQuery(id+"F4.wireOp",EDGE,"PkSCfb9l-bHuo-pSPV-febg-RSfLSyBgUNz0")])],"isStart":false});
            var sketch = newSketch(context, id + "F8", { "sketchPlane" : qUnion([Q0])});
            skLineSegment(sketch, "E222.bottom", {"start": v(-4.94, -140.75) * mm, "end": v(-5.94, -140.75) * mm});
            skLineSegment(sketch, "E222.top", {"start": v(-4.94, -208.97) * mm, "end": v(-5.94, -208.97) * mm});
            skLineSegment(sketch, "E222.left", {"start": v(-4.94, -140.75) * mm, "end": v(-4.94, -208.97) * mm});
            skLineSegment(sketch, "E222.right", {"start": v(-5.94, -140.75) * mm, "end": v(-5.94, -208.97) * mm});
            skLineSegment(sketch, "E223.bottom", {"start": v(-5.94, -208.97) * mm, "end": v(33.28, -208.97) * mm});
            skLineSegment(sketch, "E223.top", {"start": v(-5.94, -211.97) * mm, "end": v(33.28, -211.97) * mm});
            skLineSegment(sketch, "E223.left", {"start": v(-5.94, -208.97) * mm, "end": v(-5.94, -211.97) * mm});
            skLineSegment(sketch, "E223.right", {"start": v(33.28, -208.97) * mm, "end": v(33.28, -211.97) * mm});
            skLineSegment(sketch, "E224.bottom", {"start": v(33.28, -263.97) * mm, "end": v(30.28, -263.97) * mm});
            skLineSegment(sketch, "E224.top", {"start": v(33.28, -211.97) * mm, "end": v(30.28, -211.97) * mm});
            skLineSegment(sketch, "E224.left", {"start": v(33.28, -263.97) * mm, "end": v(33.28, -211.97) * mm});
            skLineSegment(sketch, "E224.right", {"start": v(30.28, -263.97) * mm, "end": v(30.28, -211.97) * mm});
            skLineSegment(sketch, "E225.bottom", {"start": v(182.06, -140.75) * mm, "end": v(183.06, -140.75) * mm});
            skLineSegment(sketch, "E225.top", {"start": v(182.06, -263.97) * mm, "end": v(183.06, -263.97) * mm});
            skLineSegment(sketch, "E225.left", {"start": v(182.06, -140.75) * mm, "end": v(182.06, -263.97) * mm});
            skLineSegment(sketch, "E225.right", {"start": v(183.06, -140.75) * mm, "end": v(183.06, -263.97) * mm});
            skLineSegment(sketch, "E226.bottom", {"start": v(183.06, -263.97) * mm, "end": v(169.06, -263.97) * mm});
            skLineSegment(sketch, "E226.top", {"start": v(183.06, -266.97) * mm, "end": v(169.06, -266.97) * mm});
            skLineSegment(sketch, "E226.left", {"start": v(183.06, -263.97) * mm, "end": v(183.06, -266.97) * mm});
            skLineSegment(sketch, "E226.right", {"start": v(169.06, -263.97) * mm, "end": v(169.06, -266.97) * mm});
            skLineSegment(sketch, "E227.bottom", {"start": v(153.56, -263.97) * mm, "end": v(118.56, -263.97) * mm});
            skLineSegment(sketch, "E227.top", {"start": v(153.56, -266.97) * mm, "end": v(118.56, -266.97) * mm});
            skLineSegment(sketch, "E227.left", {"start": v(153.56, -263.97) * mm, "end": v(153.56, -266.97) * mm});
            skLineSegment(sketch, "E227.right", {"start": v(118.56, -263.97) * mm, "end": v(118.56, -266.97) * mm});
            skLineSegment(sketch, "E228.bottom", {"start": v(30.28, -263.97) * mm, "end": v(102.28, -263.97) * mm});
            skLineSegment(sketch, "E228.top", {"start": v(30.28, -266.97) * mm, "end": v(102.28, -266.97) * mm});
            skLineSegment(sketch, "E228.left", {"start": v(30.28, -263.97) * mm, "end": v(30.28, -266.97) * mm});
            skLineSegment(sketch, "E228.right", {"start": v(102.28, -263.97) * mm, "end": v(102.28, -266.97) * mm});
            skLineSegment(sketch, "E229.bottom", {"start": v(118.56, -133.75) * mm, "end": v(119.56, -133.75) * mm});
            skLineSegment(sketch, "E229.top", {"start": v(118.56, -140.75) * mm, "end": v(119.56, -140.75) * mm});
            skLineSegment(sketch, "E229.left", {"start": v(118.56, -133.75) * mm, "end": v(118.56, -140.75) * mm});
            skLineSegment(sketch, "E229.right", {"start": v(119.56, -133.75) * mm, "end": v(119.56, -140.75) * mm});
            skLineSegment(sketch, "E230.bottom", {"start": v(58.56, -133.75) * mm, "end": v(57.56, -133.75) * mm});
            skLineSegment(sketch, "E230.top", {"start": v(58.56, -140.75) * mm, "end": v(57.56, -140.75) * mm});
            skLineSegment(sketch, "E230.left", {"start": v(58.56, -133.75) * mm, "end": v(58.56, -140.75) * mm});
            skLineSegment(sketch, "E230.right", {"start": v(57.56, -133.75) * mm, "end": v(57.56, -140.75) * mm});
            skSolve(sketch);
        }
        {
            var Q0;
            Q0 = qSketchRegion(id + "F8", true);
            extrude(context, id + "F9", {"entities" : qUnion([Q0]), "operationType" : NewBodyOperationType.ADD, "oppositeDirection" : true, "depth" : 6 * mm});
        }
        {
            var Q0;
            Q0=makeQuery(id+"F9.opExtrude","SWEPT_EDGE",EDGE,{"disambiguationData":[OSD([sQuery(id+"F8.wireOp",EDGE,"E223.top"),sQuery(id+"F8.wireOp",EDGE,"E223.left")])]});
            var Q1;
            Q1=makeQuery(id+"F9.opExtrude","SWEPT_EDGE",EDGE,{"disambiguationData":[OSD([sQuery(id+"F8.wireOp",EDGE,"E223.top"),sQuery(id+"F8.wireOp",EDGE,"E224.top"),sQuery(id+"F8.wireOp",EDGE,"E224.right")])]});
            var Q2;
            Q2=makeQuery(id+"F9.opExtrude","SWEPT_EDGE",EDGE,{"disambiguationData":[OSD([sQuery(id+"F8.wireOp",EDGE,"E228.top"),sQuery(id+"F8.wireOp",EDGE,"E228.left")])]});
            var Q3;
            Q3=makeQuery(id+"F9.opExtrude","SWEPT_EDGE",EDGE,{"disambiguationData":[OSD([sQuery(id+"F8.wireOp",EDGE,"E226.top"),sQuery(id+"F8.wireOp",EDGE,"E226.left")])]});
            fillet(context, id + "F10", {"entities" : qUnion([Q0, Q1, Q2, Q3]), "radius" : 2 * mm, "tangentPropagation" : true, "allowEdgeOverflow" : false});
        }
        {
            var Q0;
            Q0 = qSketchRegion(id + "F7", true);
            extrude(context, id + "F11", {"entities" : qUnion([Q0]), "operationType" : NewBodyOperationType.ADD, "oppositeDirection" : true, "depth" : 4 * mm});
        }
        {
            var Q0;
            {var subQ0=sQuery(id+"F4.wireOp",EDGE,"E132");var subQ1=sQuery(id+"F4.wireOp",EDGE,"E131");var subQ2=sQuery(id+"F4.wireOp",EDGE,"E130.top");Q0=makeQuery(id+"F11.boolean.opBoolean","SPLIT",FACE,{"disambiguationData":[TD([makeQuery(id+"F6.opExtrude","SWEPT_FACE",FACE,{"disambiguationData":[OSD([subQ2])]})])],"derivedFrom":makeQuery(id+"F6.opExtrude","CAP_FACE",FACE,{"disambiguationData":[OSD([sQuery(id+"F4.wireOp",EDGE,"E46.bottom"),sQuery(id+"F4.wireOp",EDGE,"E46.top"),sQuery(id+"F4.wireOp",EDGE,"E46.left"),sQuery(id+"F4.wireOp",EDGE,"E46.right"),sQuery(id+"F4.wireOp",EDGE,"E47"),sQuery(id+"F4.wireOp",EDGE,"E48"),sQuery(id+"F4.wireOp",EDGE,"E59"),sQuery(id+"F4.wireOp",EDGE,"E60"),sQuery(id+"F4.wireOp",EDGE,"E61"),sQuery(id+"F4.wireOp",EDGE,"E62"),sQuery(id+"F4.wireOp",EDGE,"E63"),sQuery(id+"F4.wireOp",EDGE,"E64"),sQuery(id+"F4.wireOp",EDGE,"E65"),sQuery(id+"F4.wireOp",EDGE,"E66"),sQuery(id+"F4.wireOp",EDGE,"E67"),sQuery(id+"F4.wireOp",EDGE,"E72"),sQuery(id+"F4.wireOp",EDGE,"E73"),sQuery(id+"F4.wireOp",EDGE,"E74"),sQuery(id+"F4.wireOp",EDGE,"E75"),sQuery(id+"F4.wireOp",EDGE,"E76"),sQuery(id+"F4.wireOp",EDGE,"CMYmPeaI-4HkP-dSsT-ciCo-EBNArNxvabU4"),sQuery(id+"F4.wireOp",EDGE,"UfYHLVnG-ZsXc-hSsb-096B-xReGw4xjWMuN"),sQuery(id+"F4.wireOp",EDGE,"LR1Smqzz-4zCy-jBud-aIPe-T4FdCvFcucQ2"),sQuery(id+"F4.wireOp",EDGE,"ZbBtRst9-qfY5-xJJi-duYC-lclwT5zfDQth"),sQuery(id+"F4.wireOp",EDGE,"8mlmSCBx-nmsO-8ibw-fLZu-H13SXNY5Fta6"),sQuery(id+"F4.wireOp",EDGE,"E85"),sQuery(id+"F4.wireOp",EDGE,"E86"),sQuery(id+"F4.wireOp",EDGE,"E87"),sQuery(id+"F4.wireOp",EDGE,"E88"),sQuery(id+"F4.wireOp",EDGE,"E89"),sQuery(id+"F4.wireOp",EDGE,"E90"),sQuery(id+"F4.wireOp",EDGE,"E91"),sQuery(id+"F4.wireOp",EDGE,"E92"),sQuery(id+"F4.wireOp",EDGE,"E93"),sQuery(id+"F4.wireOp",EDGE,"E94"),sQuery(id+"F4.wireOp",EDGE,"VxGM9Us5-GGZY-iukY-QufE-Hgw7Eb7M8YLq"),sQuery(id+"F4.wireOp",EDGE,"SQwhu13T-8Qlf-M2A9-FjbU-sqE2fhrdCHsq"),sQuery(id+"F4.wireOp",EDGE,"boMX5wRL-iCUG-njbD-9Rz0-iznqWW2C3mA9"),sQuery(id+"F4.wireOp",EDGE,"8wUrnrco-ptQb-soB3-ZJPL-oLVazxcvUS0h"),sQuery(id+"F4.wireOp",EDGE,"HpmNjthl-ehj3-1CQD-7Ubw-BaRG0imoQFcp"),sQuery(id+"F4.wireOp",EDGE,"E95"),sQuery(id+"F4.wireOp",EDGE,"E96"),sQuery(id+"F4.wireOp",EDGE,"E97"),sQuery(id+"F4.wireOp",EDGE,"E98"),sQuery(id+"F4.wireOp",EDGE,"E99"),sQuery(id+"F4.wireOp",EDGE,"E100"),sQuery(id+"F4.wireOp",EDGE,"E101"),sQuery(id+"F4.wireOp",EDGE,"E102"),sQuery(id+"F4.wireOp",EDGE,"E103"),sQuery(id+"F4.wireOp",EDGE,"E104"),sQuery(id+"F4.wireOp",EDGE,"E105"),sQuery(id+"F4.wireOp",EDGE,"E106"),sQuery(id+"F4.wireOp",EDGE,"E107"),sQuery(id+"F4.wireOp",EDGE,"E108"),sQuery(id+"F4.wireOp",EDGE,"E109"),sQuery(id+"F4.wireOp",EDGE,"E110"),sQuery(id+"F4.wireOp",EDGE,"E111"),sQuery(id+"F4.wireOp",EDGE,"E112"),sQuery(id+"F4.wireOp",EDGE,"E113"),sQuery(id+"F4.wireOp",EDGE,"E114"),sQuery(id+"F4.wireOp",EDGE,"E115"),sQuery(id+"F4.wireOp",EDGE,"E116"),sQuery(id+"F4.wireOp",EDGE,"E117"),sQuery(id+"F4.wireOp",EDGE,"E118"),sQuery(id+"F4.wireOp",EDGE,"E119"),sQuery(id+"F4.wireOp",EDGE,"E120"),sQuery(id+"F4.wireOp",EDGE,"E121"),sQuery(id+"F4.wireOp",EDGE,"E122"),sQuery(id+"F4.wireOp",EDGE,"E123"),sQuery(id+"F4.wireOp",EDGE,"E124"),sQuery(id+"F4.wireOp",EDGE,"E125"),sQuery(id+"F4.wireOp",EDGE,"E126"),sQuery(id+"F4.wireOp",EDGE,"E127"),sQuery(id+"F4.wireOp",EDGE,"E128"),sQuery(id+"F4.wireOp",EDGE,"PkSCfb9l-bHuo-pSPV-febg-RSfLSyBgUNz0"),sQuery(id+"F4.wireOp",EDGE,"E129"),subQ2,sQuery(id+"F4.wireOp",EDGE,"E130.left"),sQuery(id+"F4.wireOp",EDGE,"E130.right"),subQ1,subQ0,sQuery(id+"F4.wireOp",EDGE,"E133"),sQuery(id+"F4.wireOp",EDGE,"E135"),sQuery(id+"F4.wireOp",EDGE,"E136"),sQuery(id+"F4.wireOp",EDGE,"E137"),sQuery(id+"F4.wireOp",EDGE,"E138"),sQuery(id+"F4.wireOp",EDGE,"E139"),sQuery(id+"F4.wireOp",EDGE,"E140"),sQuery(id+"F4.wireOp",EDGE,"E141"),sQuery(id+"F4.wireOp",EDGE,"E143"),sQuery(id+"F4.wireOp",EDGE,"E144"),sQuery(id+"F4.wireOp",EDGE,"E145"),sQuery(id+"F4.wireOp",EDGE,"E146"),sQuery(id+"F4.wireOp",EDGE,"E147"),sQuery(id+"F4.wireOp",EDGE,"E148"),sQuery(id+"F4.wireOp",EDGE,"E149"),sQuery(id+"F4.wireOp",EDGE,"E150"),sQuery(id+"F4.wireOp",EDGE,"E151"),sQuery(id+"F4.wireOp",EDGE,"E152"),sQuery(id+"F4.wireOp",EDGE,"E153"),sQuery(id+"F4.wireOp",EDGE,"E154"),sQuery(id+"F4.wireOp",EDGE,"E155")])],"isStart":true})});}
            extrude(context, id + "F12", {"entities" : qUnion([Q0]), "operationType" : NewBodyOperationType.ADD, "depth" : 4 * mm});
        }
    });
